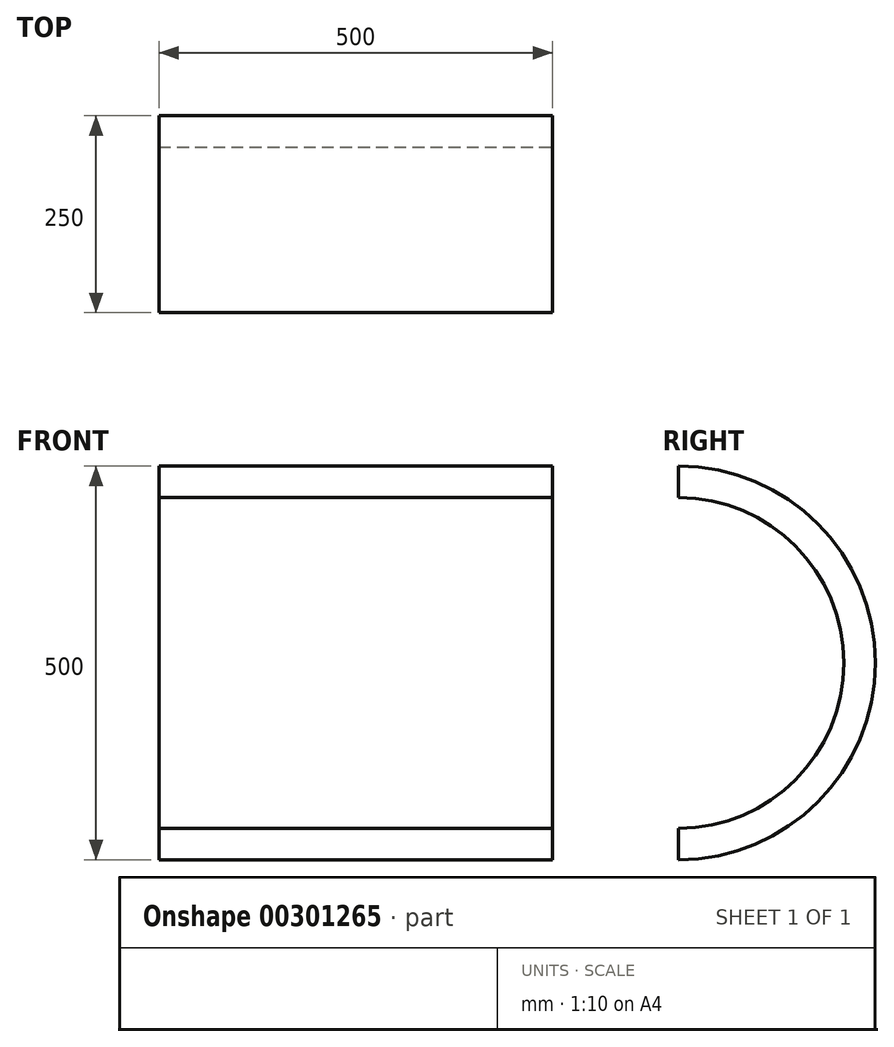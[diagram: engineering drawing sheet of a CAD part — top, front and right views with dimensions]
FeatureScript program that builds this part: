
annotation { "Feature Type Name" : "Feature", "Feature Type Description" : "" }
export const myFeature = defineFeature(function(context is Context, id is Id, definition is map)
    precondition{}
    {
        {
            var Q0;
            Q0=qCreatedBy(makeId("Right.planeOp"),FACE);
            var sketch = newSketch(context, id + "F0", { "sketchPlane" : qUnion([Q0])});
            skArc(sketch, "E0", {"start": v(0, 500) * mm, "mid": v(250, 250) * mm, "end": v(0, 0) * mm});
            skLineSegment(sketch, "E1", {"start": v(0, 500) * mm, "end": v(0, 460) * mm});
            skLineSegment(sketch, "E2", {"start": v(0, 0) * mm, "end": v(0, 40) * mm});
            skArc(sketch, "E3", {"start": v(0, 40) * mm, "mid": v(210, 250) * mm, "end": v(0, 460) * mm});
            skSolve(sketch);
        }
        {
            var Q0;
            Q0 = qSketchRegion(id + "F0", true);
            extrude(context, id + "F1", {"entities" : qUnion([Q0]), "oppositeDirection" : true, "depth" : 500 * mm});
        }
    });
